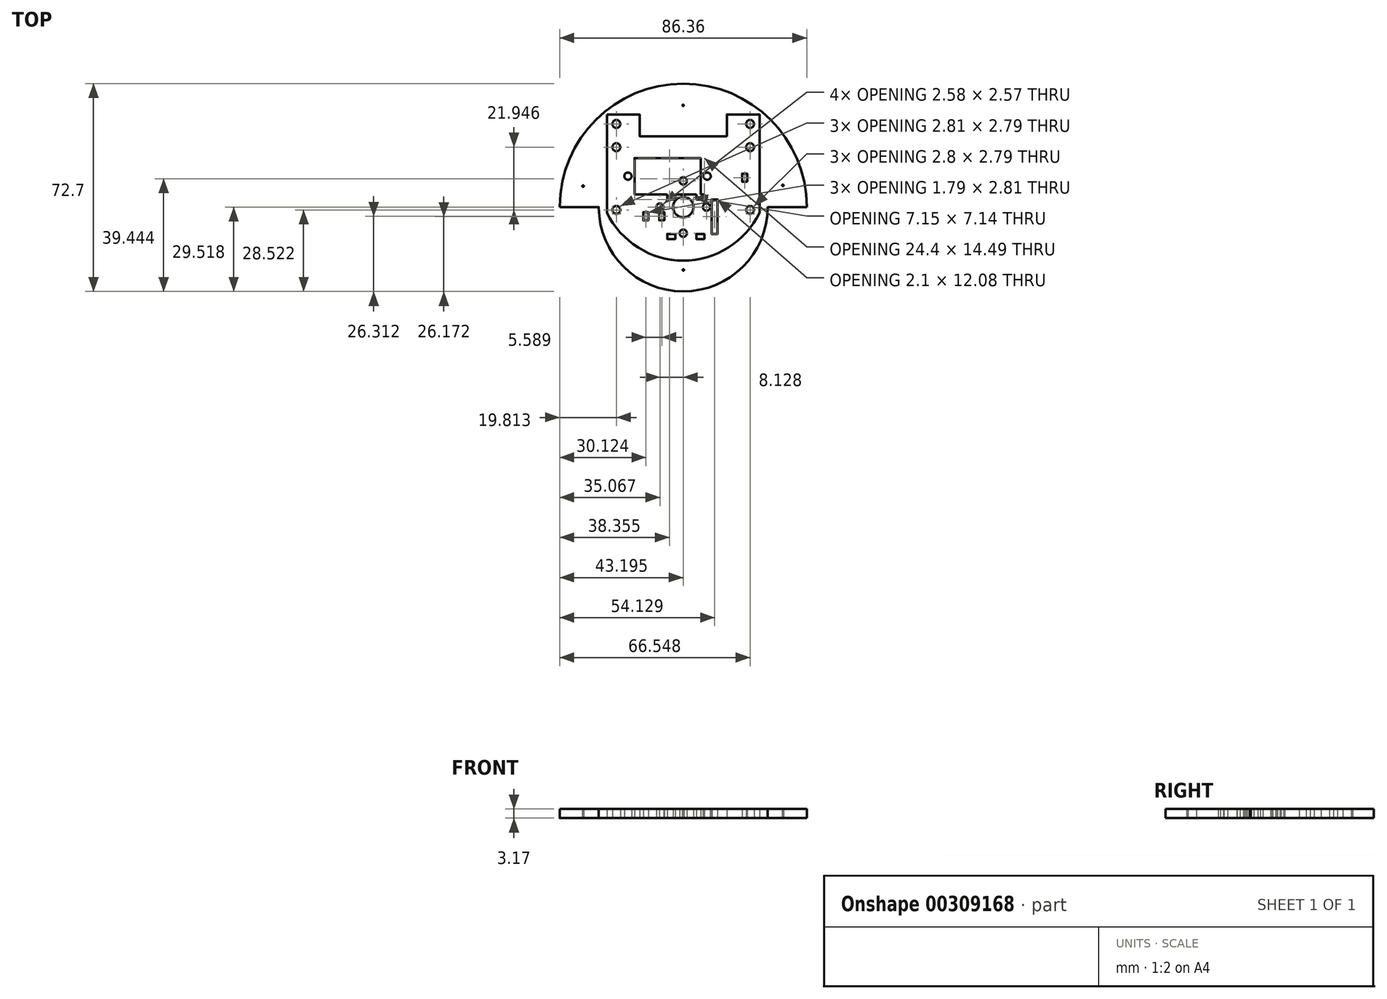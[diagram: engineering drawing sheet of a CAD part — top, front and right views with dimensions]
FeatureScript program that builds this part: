
annotation { "Feature Type Name" : "Feature", "Feature Type Description" : "" }
export const myFeature = defineFeature(function(context is Context, id is Id, definition is map)
    precondition{}
    {
        {
            var Q0;
            Q0=qCreatedBy(makeId("Top.planeOp"),FACE);
            var sketch = newSketch(context, id + "F0", { "sketchPlane" : qUnion([Q0])});
            skArc(sketch, "E0", {"start": v(0.23, 28.75) * mm, "mid": v(-0.02, 29) * mm, "end": v(-0.28, 28.75) * mm});
            skArc(sketch, "E1", {"start": v(0.22, 28.75) * mm, "mid": v(0.23, 28.75) * mm, "end": v(0.24, 28.75) * mm});
            skArc(sketch, "E2", {"start": v(0.24, 28.75) * mm, "mid": v(0.23, 28.76) * mm, "end": v(0.22, 28.75) * mm});
            skArc(sketch, "E3", {"start": v(-0.28, 28.75) * mm, "mid": v(-0.28, 28.75) * mm, "end": v(-0.27, 28.75) * mm});
            skArc(sketch, "E4", {"start": v(-0.27, 28.75) * mm, "mid": v(-0.28, 28.76) * mm, "end": v(-0.28, 28.75) * mm});
            skArc(sketch, "E5", {"start": v(-0.28, 28.75) * mm, "mid": v(-0.02, 28.5) * mm, "end": v(0.23, 28.75) * mm});
            skArc(sketch, "E6", {"start": v(3.58, -6.83) * mm, "mid": v(0.01, -3.26) * mm, "end": v(-3.55, -6.83) * mm});
            skArc(sketch, "E7", {"start": v(3.58, -6.83) * mm, "mid": v(3.58, -6.84) * mm, "end": v(3.6, -6.83) * mm});
            skArc(sketch, "E8", {"start": v(3.6, -6.83) * mm, "mid": v(3.58, -6.82) * mm, "end": v(3.58, -6.83) * mm});
            skArc(sketch, "E9", {"start": v(-3.56, -6.83) * mm, "mid": v(-3.55, -6.84) * mm, "end": v(-3.55, -6.83) * mm});
            skArc(sketch, "E10", {"start": v(-3.55, -6.83) * mm, "mid": v(-3.55, -6.83) * mm, "end": v(-3.56, -6.83) * mm});
            skArc(sketch, "E11", {"start": v(-3.55, -6.83) * mm, "mid": v(0.01, -10.4) * mm, "end": v(3.58, -6.83) * mm});
            skArc(sketch, "E12", {"start": v(35.08, 0.79) * mm, "mid": v(34.82, 1.04) * mm, "end": v(34.57, 0.79) * mm});
            skArc(sketch, "E13", {"start": v(35.07, 0.79) * mm, "mid": v(35.08, 0.78) * mm, "end": v(35.08, 0.79) * mm});
            skArc(sketch, "E14", {"start": v(35.08, 0.79) * mm, "mid": v(35.08, 0.8) * mm, "end": v(35.07, 0.79) * mm});
            skArc(sketch, "E15", {"start": v(34.57, 0.79) * mm, "mid": v(34.57, 0.78) * mm, "end": v(34.58, 0.79) * mm});
            skArc(sketch, "E16", {"start": v(34.58, 0.79) * mm, "mid": v(34.57, 0.8) * mm, "end": v(34.57, 0.79) * mm});
            skArc(sketch, "E17", {"start": v(34.57, 0.79) * mm, "mid": v(34.82, 0.53) * mm, "end": v(35.08, 0.79) * mm});
            skArc(sketch, "E18", {"start": v(-34.72, 0.5) * mm, "mid": v(-34.97, 0.76) * mm, "end": v(-35.23, 0.5) * mm});
            skArc(sketch, "E19", {"start": v(-34.73, 0.5) * mm, "mid": v(-34.72, 0.5) * mm, "end": v(-34.72, 0.5) * mm});
            skArc(sketch, "E20", {"start": v(-34.72, 0.5) * mm, "mid": v(-34.72, 0.51) * mm, "end": v(-34.73, 0.5) * mm});
            skArc(sketch, "E21", {"start": v(-35.23, 0.5) * mm, "mid": v(-35.23, 0.5) * mm, "end": v(-35.22, 0.5) * mm});
            skArc(sketch, "E22", {"start": v(-35.22, 0.5) * mm, "mid": v(-35.23, 0.51) * mm, "end": v(-35.23, 0.5) * mm});
            skArc(sketch, "E23", {"start": v(-35.23, 0.5) * mm, "mid": v(-34.97, 0.25) * mm, "end": v(-34.72, 0.5) * mm});
            skArc(sketch, "E24", {"start": v(1.3, 2.31) * mm, "mid": v(0.01, 3.6) * mm, "end": v(-1.27, 2.31) * mm});
            skArc(sketch, "E25", {"start": v(1.3, 2.31) * mm, "mid": v(1.3, 2.3) * mm, "end": v(1.3, 2.31) * mm});
            skArc(sketch, "E26", {"start": v(1.3, 2.31) * mm, "mid": v(1.3, 2.32) * mm, "end": v(1.3, 2.31) * mm});
            skArc(sketch, "E27", {"start": v(-1.27, 2.31) * mm, "mid": v(-1.27, 2.3) * mm, "end": v(-1.26, 2.31) * mm});
            skArc(sketch, "E28", {"start": v(-1.26, 2.31) * mm, "mid": v(-1.27, 2.32) * mm, "end": v(-1.27, 2.31) * mm});
            skArc(sketch, "E29", {"start": v(-1.27, 2.31) * mm, "mid": v(0.01, 1.03) * mm, "end": v(1.3, 2.31) * mm});
            skArc(sketch, "E30", {"start": v(9.42, -6.83) * mm, "mid": v(8.14, -5.55) * mm, "end": v(6.86, -6.83) * mm});
            skArc(sketch, "E31", {"start": v(9.42, -6.83) * mm, "mid": v(9.43, -6.84) * mm, "end": v(9.43, -6.83) * mm});
            skArc(sketch, "E32", {"start": v(9.43, -6.83) * mm, "mid": v(9.43, -6.83) * mm, "end": v(9.42, -6.83) * mm});
            skArc(sketch, "E33", {"start": v(6.85, -6.83) * mm, "mid": v(6.86, -6.84) * mm, "end": v(6.87, -6.83) * mm});
            skArc(sketch, "E34", {"start": v(6.87, -6.83) * mm, "mid": v(6.86, -6.82) * mm, "end": v(6.85, -6.83) * mm});
            skArc(sketch, "E35", {"start": v(6.86, -6.83) * mm, "mid": v(8.14, -8.12) * mm, "end": v(9.42, -6.83) * mm});
            skArc(sketch, "E36", {"start": v(1.3, -15.98) * mm, "mid": v(0.01, -14.7) * mm, "end": v(-1.27, -15.98) * mm});
            skArc(sketch, "E37", {"start": v(1.3, -15.98) * mm, "mid": v(1.3, -15.98) * mm, "end": v(1.3, -15.98) * mm});
            skArc(sketch, "E38", {"start": v(1.3, -15.98) * mm, "mid": v(1.3, -15.97) * mm, "end": v(1.3, -15.98) * mm});
            skArc(sketch, "E39", {"start": v(-1.27, -15.98) * mm, "mid": v(-1.27, -15.98) * mm, "end": v(-1.26, -15.98) * mm});
            skArc(sketch, "E40", {"start": v(-1.26, -15.98) * mm, "mid": v(-1.27, -15.97) * mm, "end": v(-1.27, -15.98) * mm});
            skArc(sketch, "E41", {"start": v(-1.27, -15.98) * mm, "mid": v(0.01, -17.26) * mm, "end": v(1.3, -15.98) * mm});
            skArc(sketch, "E42", {"start": v(-6.83, -6.83) * mm, "mid": v(-8.11, -5.55) * mm, "end": v(-9.4, -6.83) * mm});
            skArc(sketch, "E43", {"start": v(-6.84, -6.83) * mm, "mid": v(-6.83, -6.84) * mm, "end": v(-6.82, -6.83) * mm});
            skArc(sketch, "E44", {"start": v(-6.82, -6.83) * mm, "mid": v(-6.83, -6.83) * mm, "end": v(-6.84, -6.83) * mm});
            skArc(sketch, "E45", {"start": v(-9.4, -6.83) * mm, "mid": v(-9.4, -6.84) * mm, "end": v(-9.39, -6.83) * mm});
            skArc(sketch, "E46", {"start": v(-9.39, -6.83) * mm, "mid": v(-9.4, -6.83) * mm, "end": v(-9.4, -6.83) * mm});
            skArc(sketch, "E47", {"start": v(-9.4, -6.83) * mm, "mid": v(-8.11, -8.12) * mm, "end": v(-6.83, -6.83) * mm});
            skArc(sketch, "E48", {"start": v(0.3, -28.8) * mm, "mid": v(0.05, -28.55) * mm, "end": v(-0.2, -28.8) * mm});
            skArc(sketch, "E49", {"start": v(0.3, -28.8) * mm, "mid": v(0.3, -28.81) * mm, "end": v(0.31, -28.8) * mm});
            skArc(sketch, "E50", {"start": v(0.31, -28.8) * mm, "mid": v(0.3, -28.8) * mm, "end": v(0.3, -28.8) * mm});
            skArc(sketch, "E51", {"start": v(-0.2, -28.8) * mm, "mid": v(-0.2, -28.81) * mm, "end": v(-0.2, -28.8) * mm});
            skArc(sketch, "E52", {"start": v(-0.2, -28.8) * mm, "mid": v(-0.2, -28.8) * mm, "end": v(-0.2, -28.8) * mm});
            skArc(sketch, "E53", {"start": v(-0.2, -28.8) * mm, "mid": v(0.05, -29.06) * mm, "end": v(0.3, -28.8) * mm});
            skLineSegment(sketch, "E54", {"start": v(-29.51, -6.83) * mm, "end": v(-43.18, -6.83) * mm});
            skLineSegment(sketch, "E55", {"start": v(-43.18, -6.83) * mm, "end": v(-43.18, -6.7) * mm});
            skArc(sketch, "E56", {"start": v(-43.18, -6.7) * mm, "mid": v(0, 36.35) * mm, "end": v(43.18, -6.7) * mm});
            skLineSegment(sketch, "E57", {"start": v(43.18, -6.7) * mm, "end": v(43.18, -6.83) * mm});
            skLineSegment(sketch, "E58", {"start": v(43.18, -6.83) * mm, "end": v(29.52, -6.83) * mm});
            skLineSegment(sketch, "E59", {"start": v(29.52, -6.83) * mm, "end": v(29.52, -6.96) * mm});
            skArc(sketch, "E60", {"start": v(29.52, -6.96) * mm, "mid": v(0, -36.35) * mm, "end": v(-29.51, -6.96) * mm});
            skLineSegment(sketch, "E61", {"start": v(-29.51, -6.96) * mm, "end": v(-29.51, -6.83) * mm});
            skArc(sketch, "E62", {"start": v(-29.52, -6.83) * mm, "mid": v(-29.51, -6.84) * mm, "end": v(-29.5, -6.83) * mm});
            skArc(sketch, "E63", {"start": v(-29.5, -6.83) * mm, "mid": v(-29.51, -6.83) * mm, "end": v(-29.52, -6.83) * mm});
            skArc(sketch, "E64", {"start": v(-43.19, -6.83) * mm, "mid": v(-43.18, -6.84) * mm, "end": v(-43.17, -6.83) * mm});
            skArc(sketch, "E65", {"start": v(-43.17, -6.83) * mm, "mid": v(-43.18, -6.82) * mm, "end": v(-43.19, -6.83) * mm});
            skArc(sketch, "E66", {"start": v(-43.19, -6.7) * mm, "mid": v(-43.18, -6.71) * mm, "end": v(-43.17, -6.7) * mm});
            skArc(sketch, "E67", {"start": v(-43.17, -6.7) * mm, "mid": v(-43.18, -6.7) * mm, "end": v(-43.19, -6.7) * mm});
            skArc(sketch, "E68", {"start": v(43.18, -6.7) * mm, "mid": v(43.18, -6.71) * mm, "end": v(43.19, -6.7) * mm});
            skArc(sketch, "E69", {"start": v(43.19, -6.7) * mm, "mid": v(43.18, -6.7) * mm, "end": v(43.18, -6.7) * mm});
            skArc(sketch, "E70", {"start": v(43.18, -6.83) * mm, "mid": v(43.18, -6.84) * mm, "end": v(43.19, -6.83) * mm});
            skArc(sketch, "E71", {"start": v(43.19, -6.83) * mm, "mid": v(43.18, -6.83) * mm, "end": v(43.18, -6.83) * mm});
            skArc(sketch, "E72", {"start": v(29.51, -6.83) * mm, "mid": v(29.52, -6.84) * mm, "end": v(29.52, -6.83) * mm});
            skArc(sketch, "E73", {"start": v(29.52, -6.83) * mm, "mid": v(29.52, -6.83) * mm, "end": v(29.51, -6.83) * mm});
            skArc(sketch, "E74", {"start": v(29.51, -6.96) * mm, "mid": v(29.52, -6.97) * mm, "end": v(29.52, -6.96) * mm});
            skArc(sketch, "E75", {"start": v(29.52, -6.96) * mm, "mid": v(29.52, -6.95) * mm, "end": v(29.51, -6.96) * mm});
            skArc(sketch, "E76", {"start": v(-29.52, -6.96) * mm, "mid": v(-29.51, -6.97) * mm, "end": v(-29.5, -6.96) * mm});
            skArc(sketch, "E77", {"start": v(-29.5, -6.96) * mm, "mid": v(-29.51, -6.95) * mm, "end": v(-29.52, -6.96) * mm});
            skSolve(sketch);
        }
        {
            var Q0;
            Q0=qCreatedBy(makeId("Top.planeOp"),FACE);
            var sketch = newSketch(context, id + "F1", { "sketchPlane" : qUnion([Q0])});
            skArc(sketch, "E78", {"start": v(-18.03, 3.98) * mm, "mid": v(-19.3, 5.25) * mm, "end": v(-20.57, 3.98) * mm});
            skArc(sketch, "E79", {"start": v(-18.04, 3.98) * mm, "mid": v(-18.03, 3.98) * mm, "end": v(-18.03, 3.98) * mm});
            skArc(sketch, "E80", {"start": v(-18.03, 3.98) * mm, "mid": v(-18.03, 3.99) * mm, "end": v(-18.04, 3.98) * mm});
            skArc(sketch, "E81", {"start": v(-20.58, 3.98) * mm, "mid": v(-20.57, 3.98) * mm, "end": v(-20.57, 3.98) * mm});
            skArc(sketch, "E82", {"start": v(-20.57, 3.98) * mm, "mid": v(-20.57, 3.99) * mm, "end": v(-20.58, 3.98) * mm});
            skArc(sketch, "E83", {"start": v(-20.57, 3.98) * mm, "mid": v(-19.3, 2.71) * mm, "end": v(-18.03, 3.98) * mm});
            skArc(sketch, "E84", {"start": v(-21.97, 14.12) * mm, "mid": v(-23.37, 15.51) * mm, "end": v(-24.77, 14.12) * mm});
            skArc(sketch, "E85", {"start": v(-21.98, 14.12) * mm, "mid": v(-21.97, 14.11) * mm, "end": v(-21.96, 14.12) * mm});
            skArc(sketch, "E86", {"start": v(-21.96, 14.12) * mm, "mid": v(-21.97, 14.12) * mm, "end": v(-21.98, 14.12) * mm});
            skArc(sketch, "E87", {"start": v(-24.77, 14.12) * mm, "mid": v(-24.76, 14.11) * mm, "end": v(-24.76, 14.12) * mm});
            skArc(sketch, "E88", {"start": v(-24.76, 14.12) * mm, "mid": v(-24.76, 14.12) * mm, "end": v(-24.77, 14.12) * mm});
            skArc(sketch, "E89", {"start": v(-24.77, 14.12) * mm, "mid": v(-23.37, 12.72) * mm, "end": v(-21.97, 14.12) * mm});
            skArc(sketch, "E90", {"start": v(-21.97, -7.83) * mm, "mid": v(-23.37, -6.43) * mm, "end": v(-24.77, -7.83) * mm});
            skArc(sketch, "E91", {"start": v(-21.98, -7.83) * mm, "mid": v(-21.97, -7.83) * mm, "end": v(-21.96, -7.83) * mm});
            skArc(sketch, "E92", {"start": v(-21.96, -7.83) * mm, "mid": v(-21.97, -7.82) * mm, "end": v(-21.98, -7.83) * mm});
            skArc(sketch, "E93", {"start": v(-24.77, -7.83) * mm, "mid": v(-24.76, -7.83) * mm, "end": v(-24.76, -7.83) * mm});
            skArc(sketch, "E94", {"start": v(-24.76, -7.83) * mm, "mid": v(-24.76, -7.82) * mm, "end": v(-24.77, -7.83) * mm});
            skArc(sketch, "E95", {"start": v(-24.77, -7.83) * mm, "mid": v(-23.37, -9.23) * mm, "end": v(-21.97, -7.83) * mm});
            skLineSegment(sketch, "E96", {"start": v(4.57, -17.99) * mm, "end": v(4.57, -16.21) * mm});
            skLineSegment(sketch, "E97", {"start": v(4.57, -16.21) * mm, "end": v(7.37, -16.21) * mm});
            skLineSegment(sketch, "E98", {"start": v(7.37, -16.21) * mm, "end": v(7.37, -17.99) * mm});
            skLineSegment(sketch, "E99", {"start": v(7.37, -17.99) * mm, "end": v(4.57, -17.99) * mm});
            skArc(sketch, "E100", {"start": v(4.57, -17.99) * mm, "mid": v(4.57, -18) * mm, "end": v(4.58, -17.99) * mm});
            skArc(sketch, "E101", {"start": v(4.58, -17.99) * mm, "mid": v(4.57, -17.98) * mm, "end": v(4.57, -17.99) * mm});
            skArc(sketch, "E102", {"start": v(4.57, -16.21) * mm, "mid": v(4.57, -16.22) * mm, "end": v(4.58, -16.21) * mm});
            skArc(sketch, "E103", {"start": v(4.58, -16.21) * mm, "mid": v(4.57, -16.2) * mm, "end": v(4.57, -16.21) * mm});
            skArc(sketch, "E104", {"start": v(7.36, -16.21) * mm, "mid": v(7.37, -16.22) * mm, "end": v(7.37, -16.21) * mm});
            skArc(sketch, "E105", {"start": v(7.37, -16.21) * mm, "mid": v(7.37, -16.2) * mm, "end": v(7.36, -16.21) * mm});
            skArc(sketch, "E106", {"start": v(7.36, -17.99) * mm, "mid": v(7.37, -18) * mm, "end": v(7.37, -17.99) * mm});
            skArc(sketch, "E107", {"start": v(7.37, -17.99) * mm, "mid": v(7.37, -17.98) * mm, "end": v(7.36, -17.99) * mm});
            skLineSegment(sketch, "E108", {"start": v(4.57, -4.15) * mm, "end": v(4.57, -2.37) * mm});
            skLineSegment(sketch, "E109", {"start": v(4.57, -2.37) * mm, "end": v(7.37, -2.37) * mm});
            skLineSegment(sketch, "E110", {"start": v(7.37, -2.37) * mm, "end": v(7.37, -4.15) * mm});
            skLineSegment(sketch, "E111", {"start": v(7.37, -4.15) * mm, "end": v(4.57, -4.15) * mm});
            skArc(sketch, "E112", {"start": v(4.57, -4.15) * mm, "mid": v(4.57, -4.15) * mm, "end": v(4.58, -4.15) * mm});
            skArc(sketch, "E113", {"start": v(4.58, -4.15) * mm, "mid": v(4.57, -4.14) * mm, "end": v(4.57, -4.15) * mm});
            skArc(sketch, "E114", {"start": v(4.57, -2.37) * mm, "mid": v(4.57, -2.37) * mm, "end": v(4.58, -2.37) * mm});
            skArc(sketch, "E115", {"start": v(4.58, -2.37) * mm, "mid": v(4.57, -2.36) * mm, "end": v(4.57, -2.37) * mm});
            skArc(sketch, "E116", {"start": v(7.36, -2.37) * mm, "mid": v(7.37, -2.38) * mm, "end": v(7.37, -2.37) * mm});
            skArc(sketch, "E117", {"start": v(7.37, -2.37) * mm, "mid": v(7.37, -2.36) * mm, "end": v(7.36, -2.37) * mm});
            skArc(sketch, "E118", {"start": v(7.36, -4.15) * mm, "mid": v(7.37, -4.15) * mm, "end": v(7.37, -4.15) * mm});
            skArc(sketch, "E119", {"start": v(7.37, -4.15) * mm, "mid": v(7.37, -4.14) * mm, "end": v(7.36, -4.15) * mm});
            skLineSegment(sketch, "E120", {"start": v(-5.59, -17.99) * mm, "end": v(-2.8, -17.99) * mm});
            skLineSegment(sketch, "E121", {"start": v(-2.8, -17.99) * mm, "end": v(-2.8, -16.21) * mm});
            skLineSegment(sketch, "E122", {"start": v(-2.8, -16.21) * mm, "end": v(-5.59, -16.21) * mm});
            skLineSegment(sketch, "E123", {"start": v(-5.59, -16.21) * mm, "end": v(-5.59, -17.99) * mm});
            skArc(sketch, "E124", {"start": v(-5.6, -17.99) * mm, "mid": v(-5.59, -18) * mm, "end": v(-5.58, -17.99) * mm});
            skArc(sketch, "E125", {"start": v(-5.58, -17.99) * mm, "mid": v(-5.59, -17.98) * mm, "end": v(-5.6, -17.99) * mm});
            skArc(sketch, "E126", {"start": v(-2.8, -17.99) * mm, "mid": v(-2.8, -18) * mm, "end": v(-2.79, -17.99) * mm});
            skArc(sketch, "E127", {"start": v(-2.79, -17.99) * mm, "mid": v(-2.8, -17.98) * mm, "end": v(-2.8, -17.99) * mm});
            skArc(sketch, "E128", {"start": v(-2.8, -16.21) * mm, "mid": v(-2.8, -16.22) * mm, "end": v(-2.79, -16.21) * mm});
            skArc(sketch, "E129", {"start": v(-2.79, -16.21) * mm, "mid": v(-2.8, -16.2) * mm, "end": v(-2.8, -16.21) * mm});
            skArc(sketch, "E130", {"start": v(-5.6, -16.21) * mm, "mid": v(-5.59, -16.22) * mm, "end": v(-5.58, -16.21) * mm});
            skArc(sketch, "E131", {"start": v(-5.58, -16.21) * mm, "mid": v(-5.59, -16.2) * mm, "end": v(-5.6, -16.21) * mm});
            skLineSegment(sketch, "E132", {"start": v(-5.59, -4.15) * mm, "end": v(-2.8, -4.15) * mm});
            skLineSegment(sketch, "E133", {"start": v(-2.8, -4.15) * mm, "end": v(-2.8, -2.37) * mm});
            skLineSegment(sketch, "E134", {"start": v(-2.8, -2.37) * mm, "end": v(-5.59, -2.37) * mm});
            skLineSegment(sketch, "E135", {"start": v(-5.59, -2.37) * mm, "end": v(-5.59, -4.15) * mm});
            skArc(sketch, "E136", {"start": v(-5.6, -4.15) * mm, "mid": v(-5.59, -4.15) * mm, "end": v(-5.58, -4.15) * mm});
            skArc(sketch, "E137", {"start": v(-5.58, -4.15) * mm, "mid": v(-5.59, -4.14) * mm, "end": v(-5.6, -4.15) * mm});
            skArc(sketch, "E138", {"start": v(-2.8, -4.15) * mm, "mid": v(-2.8, -4.15) * mm, "end": v(-2.79, -4.15) * mm});
            skArc(sketch, "E139", {"start": v(-2.79, -4.15) * mm, "mid": v(-2.8, -4.14) * mm, "end": v(-2.8, -4.15) * mm});
            skArc(sketch, "E140", {"start": v(-2.8, -2.37) * mm, "mid": v(-2.8, -2.37) * mm, "end": v(-2.79, -2.37) * mm});
            skArc(sketch, "E141", {"start": v(-2.79, -2.37) * mm, "mid": v(-2.8, -2.36) * mm, "end": v(-2.8, -2.37) * mm});
            skArc(sketch, "E142", {"start": v(-5.6, -2.37) * mm, "mid": v(-5.59, -2.37) * mm, "end": v(-5.58, -2.37) * mm});
            skArc(sketch, "E143", {"start": v(-5.58, -2.37) * mm, "mid": v(-5.59, -2.36) * mm, "end": v(-5.6, -2.37) * mm});
            skLineSegment(sketch, "E144", {"start": v(10.08, -16.21) * mm, "end": v(9.9, -16.21) * mm});
            skLineSegment(sketch, "E145", {"start": v(9.9, -16.21) * mm, "end": v(9.9, -4.15) * mm});
            skLineSegment(sketch, "E146", {"start": v(9.9, -4.15) * mm, "end": v(11.99, -4.15) * mm});
            skLineSegment(sketch, "E147", {"start": v(11.99, -4.15) * mm, "end": v(11.99, -16.21) * mm});
            skLineSegment(sketch, "E148", {"start": v(11.99, -16.21) * mm, "end": v(10.08, -16.21) * mm});
            skArc(sketch, "E149", {"start": v(10.08, -16.21) * mm, "mid": v(10.08, -16.22) * mm, "end": v(10.1, -16.21) * mm});
            skArc(sketch, "E150", {"start": v(10.1, -16.21) * mm, "mid": v(10.08, -16.2) * mm, "end": v(10.08, -16.21) * mm});
            skArc(sketch, "E151", {"start": v(9.9, -16.21) * mm, "mid": v(9.9, -16.22) * mm, "end": v(9.91, -16.21) * mm});
            skArc(sketch, "E152", {"start": v(9.91, -16.21) * mm, "mid": v(9.9, -16.2) * mm, "end": v(9.9, -16.21) * mm});
            skArc(sketch, "E153", {"start": v(9.9, -4.15) * mm, "mid": v(9.9, -4.15) * mm, "end": v(9.91, -4.15) * mm});
            skArc(sketch, "E154", {"start": v(9.91, -4.15) * mm, "mid": v(9.9, -4.14) * mm, "end": v(9.9, -4.15) * mm});
            skArc(sketch, "E155", {"start": v(11.98, -4.15) * mm, "mid": v(11.99, -4.15) * mm, "end": v(12, -4.15) * mm});
            skArc(sketch, "E156", {"start": v(12, -4.15) * mm, "mid": v(11.99, -4.14) * mm, "end": v(11.98, -4.15) * mm});
            skArc(sketch, "E157", {"start": v(11.98, -16.21) * mm, "mid": v(11.99, -16.22) * mm, "end": v(12, -16.21) * mm});
            skArc(sketch, "E158", {"start": v(12, -16.21) * mm, "mid": v(11.99, -16.2) * mm, "end": v(11.98, -16.21) * mm});
            skArc(sketch, "E159", {"start": v(-26.67, -8.74) * mm, "mid": v(0, -25.55) * mm, "end": v(26.67, -8.74) * mm});
            skLineSegment(sketch, "E160", {"start": v(26.67, -8.74) * mm, "end": v(26.67, 25.55) * mm});
            skLineSegment(sketch, "E161", {"start": v(26.67, 25.55) * mm, "end": v(15.24, 25.55) * mm});
            skLineSegment(sketch, "E162", {"start": v(15.24, 25.55) * mm, "end": v(15.24, 17.93) * mm});
            skLineSegment(sketch, "E163", {"start": v(15.24, 17.93) * mm, "end": v(-15.24, 17.93) * mm});
            skLineSegment(sketch, "E164", {"start": v(-15.24, 17.93) * mm, "end": v(-15.24, 25.55) * mm});
            skLineSegment(sketch, "E165", {"start": v(-15.24, 25.55) * mm, "end": v(-26.67, 25.55) * mm});
            skLineSegment(sketch, "E166", {"start": v(-26.67, 25.55) * mm, "end": v(-26.67, -8.74) * mm});
            skArc(sketch, "E167", {"start": v(-26.68, -8.74) * mm, "mid": v(-26.67, -8.75) * mm, "end": v(-26.66, -8.74) * mm});
            skArc(sketch, "E168", {"start": v(-26.66, -8.74) * mm, "mid": v(-26.67, -8.74) * mm, "end": v(-26.68, -8.74) * mm});
            skArc(sketch, "E169", {"start": v(26.66, -8.74) * mm, "mid": v(26.67, -8.75) * mm, "end": v(26.68, -8.74) * mm});
            skArc(sketch, "E170", {"start": v(26.68, -8.74) * mm, "mid": v(26.67, -8.74) * mm, "end": v(26.66, -8.74) * mm});
            skArc(sketch, "E171", {"start": v(26.66, 25.55) * mm, "mid": v(26.67, 25.54) * mm, "end": v(26.68, 25.55) * mm});
            skArc(sketch, "E172", {"start": v(26.68, 25.55) * mm, "mid": v(26.67, 25.55) * mm, "end": v(26.66, 25.55) * mm});
            skArc(sketch, "E173", {"start": v(15.23, 25.55) * mm, "mid": v(15.24, 25.54) * mm, "end": v(15.25, 25.55) * mm});
            skArc(sketch, "E174", {"start": v(15.25, 25.55) * mm, "mid": v(15.24, 25.55) * mm, "end": v(15.23, 25.55) * mm});
            skArc(sketch, "E175", {"start": v(15.23, 17.93) * mm, "mid": v(15.24, 17.92) * mm, "end": v(15.25, 17.93) * mm});
            skArc(sketch, "E176", {"start": v(15.25, 17.93) * mm, "mid": v(15.24, 17.93) * mm, "end": v(15.23, 17.93) * mm});
            skArc(sketch, "E177", {"start": v(-15.25, 17.93) * mm, "mid": v(-15.24, 17.92) * mm, "end": v(-15.23, 17.93) * mm});
            skArc(sketch, "E178", {"start": v(-15.23, 17.93) * mm, "mid": v(-15.24, 17.93) * mm, "end": v(-15.25, 17.93) * mm});
            skArc(sketch, "E179", {"start": v(-15.25, 25.55) * mm, "mid": v(-15.24, 25.54) * mm, "end": v(-15.23, 25.55) * mm});
            skArc(sketch, "E180", {"start": v(-15.23, 25.55) * mm, "mid": v(-15.24, 25.55) * mm, "end": v(-15.25, 25.55) * mm});
            skArc(sketch, "E181", {"start": v(-26.68, 25.55) * mm, "mid": v(-26.67, 25.54) * mm, "end": v(-26.66, 25.55) * mm});
            skArc(sketch, "E182", {"start": v(-26.66, 25.55) * mm, "mid": v(-26.67, 25.55) * mm, "end": v(-26.68, 25.55) * mm});
            skLineSegment(sketch, "E183", {"start": v(6.1, 10.33) * mm, "end": v(6.1, -2.37) * mm});
            skLineSegment(sketch, "E184", {"start": v(6.1, -2.37) * mm, "end": v(-17.02, -2.37) * mm});
            skLineSegment(sketch, "E185", {"start": v(-17.02, -2.37) * mm, "end": v(-17.02, 10.33) * mm});
            skLineSegment(sketch, "E186", {"start": v(-17.02, 10.33) * mm, "end": v(6.1, 10.33) * mm});
            skArc(sketch, "E187", {"start": v(6.09, 10.33) * mm, "mid": v(6.1, 10.32) * mm, "end": v(6.1, 10.33) * mm});
            skArc(sketch, "E188", {"start": v(6.1, 10.33) * mm, "mid": v(6.1, 10.34) * mm, "end": v(6.09, 10.33) * mm});
            skArc(sketch, "E189", {"start": v(6.09, -2.37) * mm, "mid": v(6.1, -2.38) * mm, "end": v(6.1, -2.37) * mm});
            skArc(sketch, "E190", {"start": v(6.1, -2.37) * mm, "mid": v(6.1, -2.36) * mm, "end": v(6.09, -2.37) * mm});
            skArc(sketch, "E191", {"start": v(-17.02, -2.37) * mm, "mid": v(-17.02, -2.37) * mm, "end": v(-17.01, -2.37) * mm});
            skArc(sketch, "E192", {"start": v(-17.01, -2.37) * mm, "mid": v(-17.02, -2.36) * mm, "end": v(-17.02, -2.37) * mm});
            skArc(sketch, "E193", {"start": v(-17.02, 10.33) * mm, "mid": v(-17.02, 10.33) * mm, "end": v(-17.01, 10.33) * mm});
            skArc(sketch, "E194", {"start": v(-17.01, 10.33) * mm, "mid": v(-17.02, 10.34) * mm, "end": v(-17.02, 10.33) * mm});
            skArc(sketch, "E195", {"start": v(9.65, 3.98) * mm, "mid": v(8.38, 5.25) * mm, "end": v(7.11, 3.98) * mm});
            skArc(sketch, "E196", {"start": v(9.65, 3.98) * mm, "mid": v(9.65, 3.98) * mm, "end": v(9.66, 3.98) * mm});
            skArc(sketch, "E197", {"start": v(9.66, 3.98) * mm, "mid": v(9.65, 3.99) * mm, "end": v(9.65, 3.98) * mm});
            skArc(sketch, "E198", {"start": v(7.1, 3.98) * mm, "mid": v(7.11, 3.97) * mm, "end": v(7.12, 3.98) * mm});
            skArc(sketch, "E199", {"start": v(7.12, 3.98) * mm, "mid": v(7.11, 4) * mm, "end": v(7.1, 3.98) * mm});
            skArc(sketch, "E200", {"start": v(7.11, 3.98) * mm, "mid": v(8.38, 2.71) * mm, "end": v(9.65, 3.98) * mm});
            skLineSegment(sketch, "E201", {"start": v(20.57, 2.08) * mm, "end": v(20.57, 4.87) * mm});
            skLineSegment(sketch, "E202", {"start": v(20.57, 4.87) * mm, "end": v(22.35, 4.87) * mm});
            skLineSegment(sketch, "E203", {"start": v(22.35, 4.87) * mm, "end": v(22.35, 2.08) * mm});
            skLineSegment(sketch, "E204", {"start": v(22.35, 2.08) * mm, "end": v(20.57, 2.08) * mm});
            skArc(sketch, "E205", {"start": v(20.57, 2.08) * mm, "mid": v(20.58, 2.07) * mm, "end": v(20.58, 2.08) * mm});
            skArc(sketch, "E206", {"start": v(20.58, 2.08) * mm, "mid": v(20.58, 2.08) * mm, "end": v(20.57, 2.08) * mm});
            skArc(sketch, "E207", {"start": v(20.57, 4.87) * mm, "mid": v(20.58, 4.87) * mm, "end": v(20.58, 4.87) * mm});
            skArc(sketch, "E208", {"start": v(20.58, 4.87) * mm, "mid": v(20.58, 4.88) * mm, "end": v(20.57, 4.87) * mm});
            skArc(sketch, "E209", {"start": v(22.35, 4.87) * mm, "mid": v(22.35, 4.87) * mm, "end": v(22.36, 4.87) * mm});
            skArc(sketch, "E210", {"start": v(22.36, 4.87) * mm, "mid": v(22.35, 4.88) * mm, "end": v(22.35, 4.87) * mm});
            skArc(sketch, "E211", {"start": v(22.35, 2.08) * mm, "mid": v(22.35, 2.07) * mm, "end": v(22.36, 2.08) * mm});
            skArc(sketch, "E212", {"start": v(22.36, 2.08) * mm, "mid": v(22.35, 2.08) * mm, "end": v(22.35, 2.08) * mm});
            skLineSegment(sketch, "E213", {"start": v(-8.36, -11.44) * mm, "end": v(-6.58, -11.44) * mm});
            skLineSegment(sketch, "E214", {"start": v(-6.58, -11.44) * mm, "end": v(-6.58, -8.64) * mm});
            skLineSegment(sketch, "E215", {"start": v(-6.58, -8.64) * mm, "end": v(-8.36, -8.64) * mm});
            skLineSegment(sketch, "E216", {"start": v(-8.36, -8.64) * mm, "end": v(-8.36, -11.44) * mm});
            skArc(sketch, "E217", {"start": v(-8.36, -11.44) * mm, "mid": v(-8.36, -11.44) * mm, "end": v(-8.35, -11.44) * mm});
            skArc(sketch, "E218", {"start": v(-8.35, -11.44) * mm, "mid": v(-8.36, -11.43) * mm, "end": v(-8.36, -11.44) * mm});
            skArc(sketch, "E219", {"start": v(-6.58, -11.44) * mm, "mid": v(-6.58, -11.44) * mm, "end": v(-6.57, -11.44) * mm});
            skArc(sketch, "E220", {"start": v(-6.57, -11.44) * mm, "mid": v(-6.58, -11.43) * mm, "end": v(-6.58, -11.44) * mm});
            skArc(sketch, "E221", {"start": v(-6.58, -8.64) * mm, "mid": v(-6.58, -8.65) * mm, "end": v(-6.57, -8.64) * mm});
            skArc(sketch, "E222", {"start": v(-6.57, -8.64) * mm, "mid": v(-6.58, -8.63) * mm, "end": v(-6.58, -8.64) * mm});
            skArc(sketch, "E223", {"start": v(-8.36, -8.64) * mm, "mid": v(-8.36, -8.65) * mm, "end": v(-8.35, -8.64) * mm});
            skArc(sketch, "E224", {"start": v(-8.35, -8.64) * mm, "mid": v(-8.36, -8.64) * mm, "end": v(-8.36, -8.64) * mm});
            skLineSegment(sketch, "E225", {"start": v(-13.94, -11.44) * mm, "end": v(-12.17, -11.44) * mm});
            skLineSegment(sketch, "E226", {"start": v(-12.17, -11.44) * mm, "end": v(-12.17, -8.64) * mm});
            skLineSegment(sketch, "E227", {"start": v(-12.17, -8.64) * mm, "end": v(-13.94, -8.64) * mm});
            skLineSegment(sketch, "E228", {"start": v(-13.94, -8.64) * mm, "end": v(-13.94, -11.44) * mm});
            skArc(sketch, "E229", {"start": v(-13.95, -11.44) * mm, "mid": v(-13.94, -11.44) * mm, "end": v(-13.94, -11.44) * mm});
            skArc(sketch, "E230", {"start": v(-13.94, -11.44) * mm, "mid": v(-13.94, -11.43) * mm, "end": v(-13.95, -11.44) * mm});
            skArc(sketch, "E231", {"start": v(-12.17, -11.44) * mm, "mid": v(-12.17, -11.44) * mm, "end": v(-12.16, -11.44) * mm});
            skArc(sketch, "E232", {"start": v(-12.16, -11.44) * mm, "mid": v(-12.17, -11.43) * mm, "end": v(-12.17, -11.44) * mm});
            skArc(sketch, "E233", {"start": v(-12.17, -8.64) * mm, "mid": v(-12.17, -8.65) * mm, "end": v(-12.16, -8.64) * mm});
            skArc(sketch, "E234", {"start": v(-12.16, -8.64) * mm, "mid": v(-12.17, -8.64) * mm, "end": v(-12.17, -8.64) * mm});
            skArc(sketch, "E235", {"start": v(-13.95, -8.64) * mm, "mid": v(-13.94, -8.65) * mm, "end": v(-13.94, -8.64) * mm});
            skArc(sketch, "E236", {"start": v(-13.94, -8.64) * mm, "mid": v(-13.94, -8.63) * mm, "end": v(-13.95, -8.64) * mm});
            skArc(sketch, "E237", {"start": v(24.77, 22.25) * mm, "mid": v(23.37, 23.64) * mm, "end": v(21.97, 22.25) * mm});
            skArc(sketch, "E238", {"start": v(24.76, 22.25) * mm, "mid": v(24.77, 22.24) * mm, "end": v(24.77, 22.25) * mm});
            skArc(sketch, "E239", {"start": v(24.77, 22.25) * mm, "mid": v(24.77, 22.25) * mm, "end": v(24.76, 22.25) * mm});
            skArc(sketch, "E240", {"start": v(21.97, 22.25) * mm, "mid": v(21.97, 22.24) * mm, "end": v(21.98, 22.25) * mm});
            skArc(sketch, "E241", {"start": v(21.98, 22.25) * mm, "mid": v(21.97, 22.25) * mm, "end": v(21.97, 22.25) * mm});
            skArc(sketch, "E242", {"start": v(21.97, 22.25) * mm, "mid": v(23.37, 20.85) * mm, "end": v(24.77, 22.25) * mm});
            skArc(sketch, "E243", {"start": v(-21.97, 22.25) * mm, "mid": v(-23.37, 23.64) * mm, "end": v(-24.77, 22.25) * mm});
            skArc(sketch, "E244", {"start": v(-21.98, 22.25) * mm, "mid": v(-21.97, 22.24) * mm, "end": v(-21.96, 22.25) * mm});
            skArc(sketch, "E245", {"start": v(-21.96, 22.25) * mm, "mid": v(-21.97, 22.25) * mm, "end": v(-21.98, 22.25) * mm});
            skArc(sketch, "E246", {"start": v(-24.77, 22.25) * mm, "mid": v(-24.76, 22.24) * mm, "end": v(-24.76, 22.25) * mm});
            skArc(sketch, "E247", {"start": v(-24.76, 22.25) * mm, "mid": v(-24.76, 22.25) * mm, "end": v(-24.77, 22.25) * mm});
            skArc(sketch, "E248", {"start": v(-24.77, 22.25) * mm, "mid": v(-23.37, 20.85) * mm, "end": v(-21.97, 22.25) * mm});
            skArc(sketch, "E249", {"start": v(24.77, -7.83) * mm, "mid": v(23.37, -6.43) * mm, "end": v(21.97, -7.83) * mm});
            skArc(sketch, "E250", {"start": v(24.76, -7.83) * mm, "mid": v(24.77, -7.83) * mm, "end": v(24.77, -7.83) * mm});
            skArc(sketch, "E251", {"start": v(24.77, -7.83) * mm, "mid": v(24.77, -7.82) * mm, "end": v(24.76, -7.83) * mm});
            skArc(sketch, "E252", {"start": v(21.97, -7.83) * mm, "mid": v(21.97, -7.83) * mm, "end": v(21.98, -7.83) * mm});
            skArc(sketch, "E253", {"start": v(21.98, -7.83) * mm, "mid": v(21.97, -7.82) * mm, "end": v(21.97, -7.83) * mm});
            skArc(sketch, "E254", {"start": v(21.97, -7.83) * mm, "mid": v(23.37, -9.23) * mm, "end": v(24.77, -7.83) * mm});
            skArc(sketch, "E255", {"start": v(24.77, 14.12) * mm, "mid": v(23.37, 15.51) * mm, "end": v(21.97, 14.12) * mm});
            skArc(sketch, "E256", {"start": v(24.76, 14.12) * mm, "mid": v(24.77, 14.11) * mm, "end": v(24.77, 14.12) * mm});
            skArc(sketch, "E257", {"start": v(24.77, 14.12) * mm, "mid": v(24.77, 14.12) * mm, "end": v(24.76, 14.12) * mm});
            skArc(sketch, "E258", {"start": v(21.97, 14.12) * mm, "mid": v(21.97, 14.11) * mm, "end": v(21.98, 14.12) * mm});
            skArc(sketch, "E259", {"start": v(21.98, 14.12) * mm, "mid": v(21.97, 14.12) * mm, "end": v(21.97, 14.12) * mm});
            skArc(sketch, "E260", {"start": v(21.97, 14.12) * mm, "mid": v(23.37, 12.72) * mm, "end": v(24.77, 14.12) * mm});
            skSolve(sketch);
        }
        {
            var Q0;
            {var subQ107=sQuery(id+"F0.wireOp",EDGE,"E73");Q0=makeQuery(id+"F0.imprint","IMPRINT",FACE,{"disambiguationData":[TD([[makeQuery(id+"F0.imprint","IMPRINT",EDGE,{"derivedFrom":subQ107}),-1.0]])]});}
            extrude(context, id + "F2", {"entities" : qUnion([Q0]), "depth" : 3.17 * mm});
        }
        {
            var Q0;
            {var subQ173=sQuery(id+"F1.wireOp",EDGE,"E103");Q0=makeQuery(id+"F1.imprint","IMPRINT",FACE,{"disambiguationData":[TD([[makeQuery(id+"F1.imprint","IMPRINT",EDGE,{"derivedFrom":subQ173}),-1.0]])]});}
            extrude(context, id + "F3", {"entities" : qUnion([Q0]), "depth" : 3.17 * mm});
        }
    });
